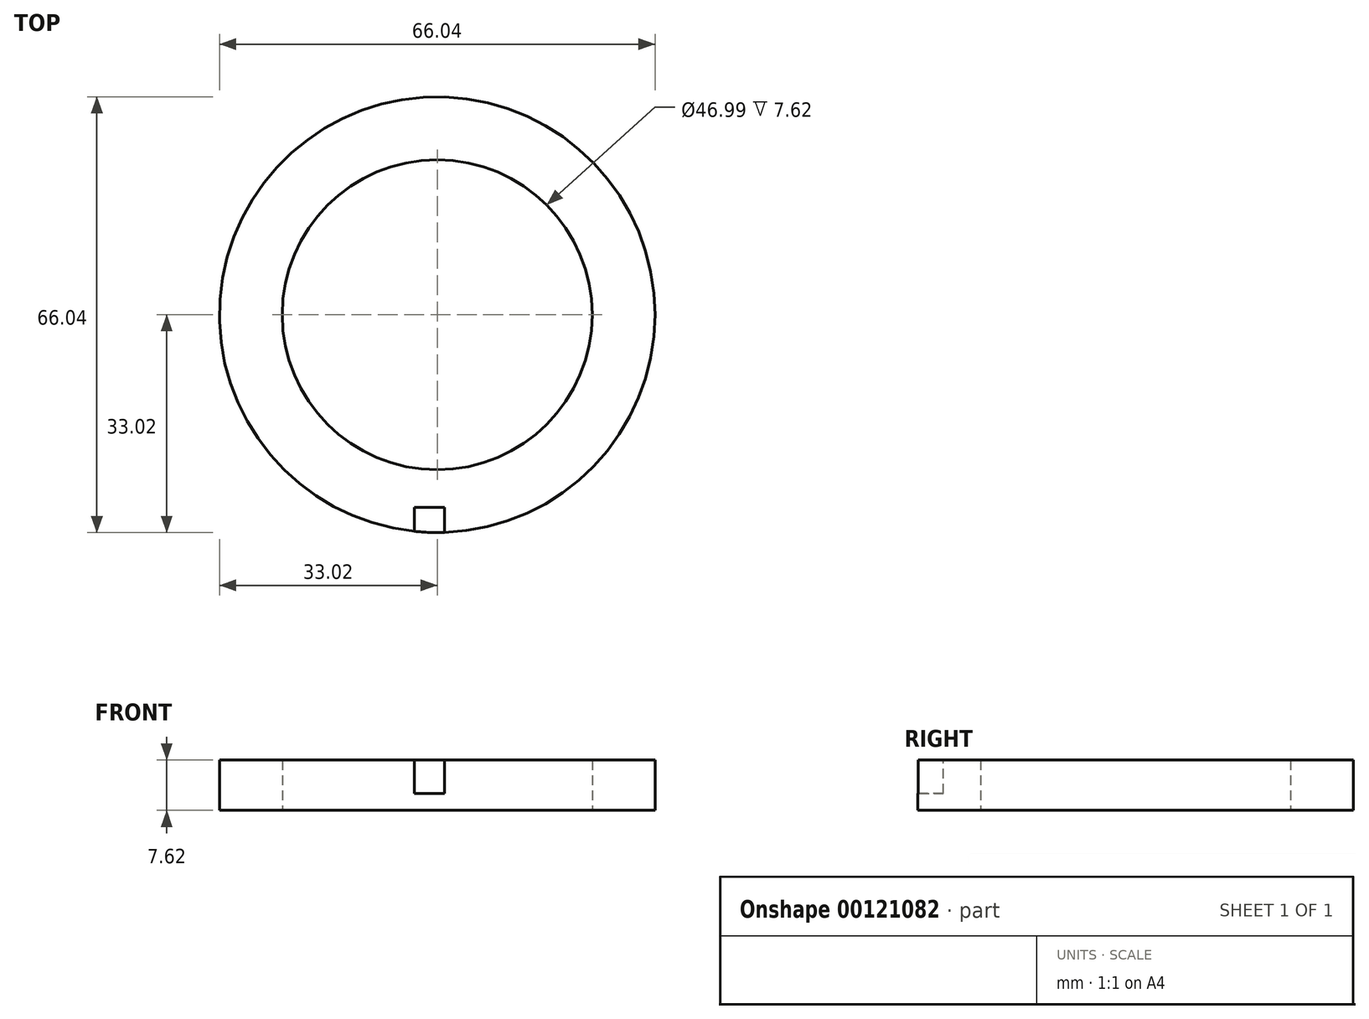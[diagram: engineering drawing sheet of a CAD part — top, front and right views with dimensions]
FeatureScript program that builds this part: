
annotation { "Feature Type Name" : "Feature", "Feature Type Description" : "" }
export const myFeature = defineFeature(function(context is Context, id is Id, definition is map)
    precondition{}
    {
        {
            var Q0;
            Q0=qCreatedBy(makeId("Top.planeOp"),FACE);
            var sketch = newSketch(context, id + "F0", { "sketchPlane" : qUnion([Q0])});
            skCircle(sketch, "E0", {"center": v(0, 0) * mm, "radius": 33.02 * mm});
            skCircle(sketch, "E1.0", {"center": v(0, 0) * mm, "radius": 23.5 * mm});
            skSolve(sketch);
        }
        {
            var Q0;
            Q0=makeQuery(id+"F0.imprint","IMPRINT",FACE,{"disambiguationData":[TD([[makeQuery(id+"F0.imprint","IMPRINT",EDGE,{"derivedFrom":sQuery(id+"F0.wireOp",EDGE,"E0")}),1.0]])]});
            extrude(context, id + "F1", {"entities" : qUnion([Q0]), "depth" : 7.62 * mm});
        }
        {
            var Q0;
            Q0=makeQuery(id+"F1.opExtrude","CAP_FACE",FACE,{"disambiguationData":[OSD([sQuery(id+"F0.wireOp",EDGE,"E0"),sQuery(id+"F0.wireOp",EDGE,"E1.0")])],"isStart":false});
            var sketch = newSketch(context, id + "F2", { "sketchPlane" : qUnion([Q0])});
            skLineSegment(sketch, "E2", {"start": v(-3.45, -32.84) * mm, "end": v(-3.45, -29.2) * mm});
            skLineSegment(sketch, "E3", {"start": v(-3.45, -29.2) * mm, "end": v(1.12, -29.2) * mm});
            skLineSegment(sketch, "E4", {"start": v(1.12, -29.2) * mm, "end": v(1.12, -33) * mm});
            skSolve(sketch);
        }
        {
            var Q0;
            Q0 = qSketchRegion(id + "F2", true);
            var Q1;
            {var subQ0=sQuery(id+"F2.wireOp",EDGE,"E2");Q1=makeQuery(id+"F2.imprint","IMPRINT",FACE,{"disambiguationData":[TD([[makeQuery(id+"F2.imprint","IMPRINT",EDGE,{"derivedFrom":subQ0}),-1.0]])]});}
            extrude(context, id + "F3", {"entities" : qUnion([Q0, Q1]), "operationType" : NewBodyOperationType.REMOVE, "oppositeDirection" : true, "depth" : 5.08 * mm});
        }
    });
